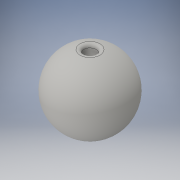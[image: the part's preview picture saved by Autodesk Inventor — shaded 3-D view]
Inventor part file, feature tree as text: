
AUTODESK INVENTOR PART (.ipt)
format: ipt  version: 2016 SP1 (Build 200210100, 210)  size: 142,848 bytes
history: native  units: in
note: dims shown in document units (in); Inventor stores cm internally (conversion verified against a paired STEP export)
features: sketch x2, revolve x1, extrude x1, fillet x1
ambient origin geometry x8: Origin, YZ Plane, XZ Plane, XY Plane, X Axis, Y Axis, Z Axis, Center Point
bodies: Body1 (feature_tree)
feature tree (5):
  revolve  "Revolution1"  Angle=90.0deg
  extrude  "Extrusion4"  Depth=0.125in
  fillet  "Fillet1"  [1 undecoded]
  sketch  "Sketch8"  dims[d25=3.0in d26=90.0deg]
  sketch  "Sketch9"  dims[d27=0.5in d28=3.0in d29=0.0in d30=0.125in]
note: 1 required parameter value undecoded (feature->parameter linkage not recoverable at this tier; creation-order binding heuristic only, values carry confidence <= 0.55)
